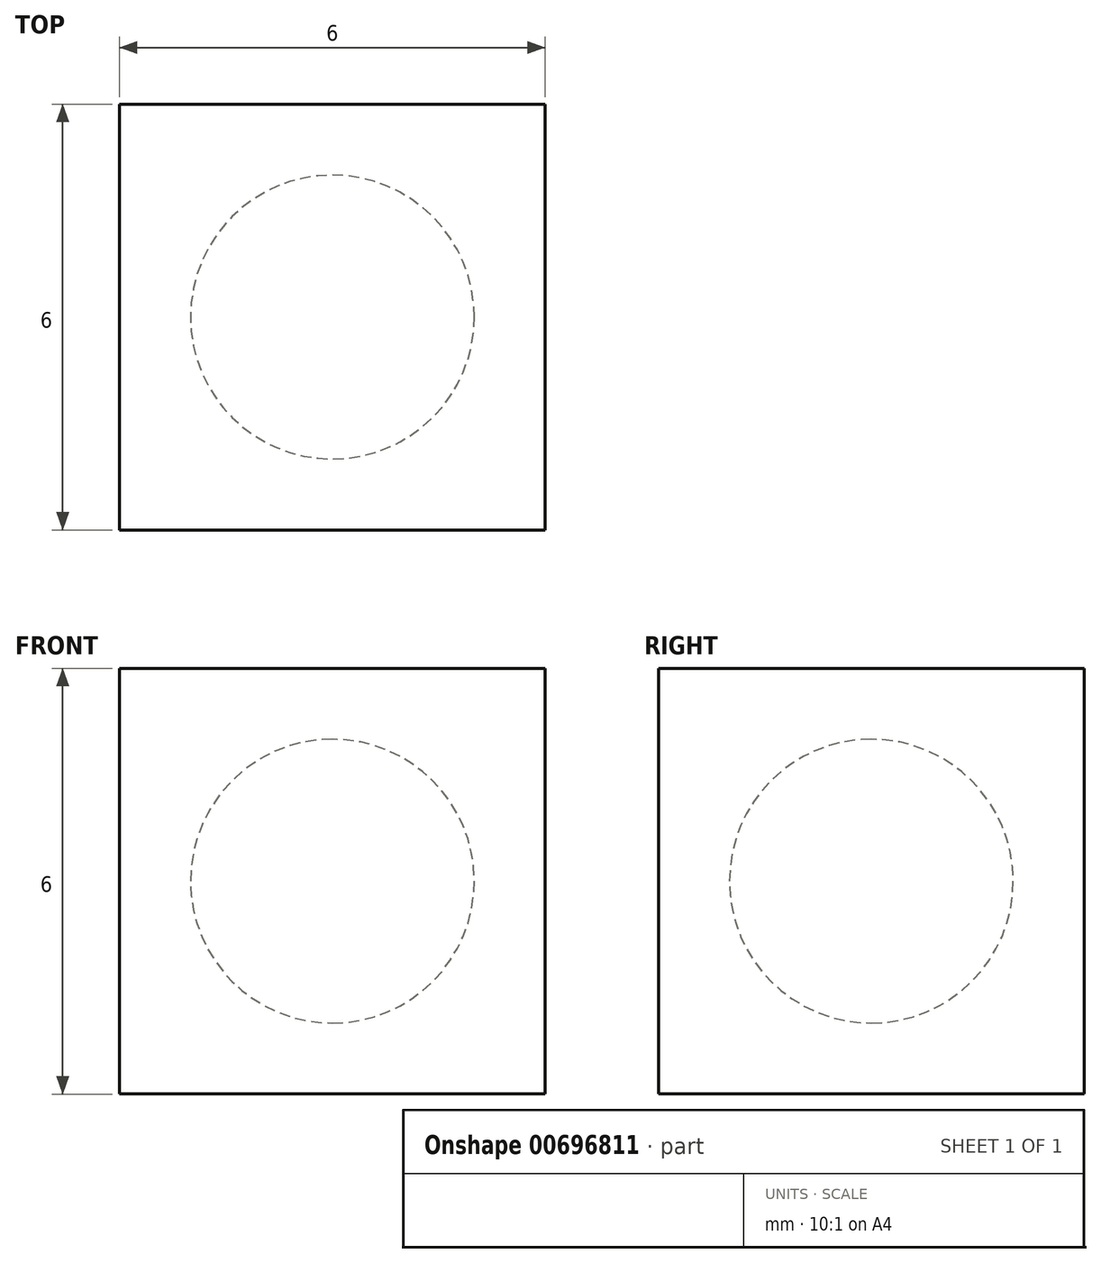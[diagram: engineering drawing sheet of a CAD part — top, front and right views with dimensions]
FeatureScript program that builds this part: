
annotation { "Feature Type Name" : "Feature", "Feature Type Description" : "" }
export const myFeature = defineFeature(function(context is Context, id is Id, definition is map)
    precondition{}
    {
        {
            var Q0;
            Q0=qCreatedBy(makeId("Front.planeOp"),FACE);
            var sketch = newSketch(context, id + "F0", { "sketchPlane" : qUnion([Q0])});
            skLineSegment(sketch, "E0.bottom", {"start": v(0.4, -1.79) * mm, "end": v(6.4, -1.79) * mm});
            skLineSegment(sketch, "E0.top", {"start": v(0.4, -7.79) * mm, "end": v(6.4, -7.79) * mm});
            skLineSegment(sketch, "E0.left", {"start": v(0.4, -1.79) * mm, "end": v(0.4, -7.79) * mm});
            skLineSegment(sketch, "E0.right", {"start": v(6.4, -1.79) * mm, "end": v(6.4, -7.79) * mm});
            skSolve(sketch);
        }
        {
            var Q0;
            Q0=makeQuery(id+"F0.imprint","IMPRINT",FACE,{"disambiguationData":[TD([[makeQuery(id+"F0.imprint","IMPRINT",EDGE,{"derivedFrom":sQuery(id+"F0.wireOp",EDGE,"E0.bottom")}),-1.0]])]});
            extrude(context, id + "F1", {"entities" : qUnion([Q0]), "depth" : 3 * mm, "offsetDistance" : 25.4 * mm});
        }
        {
            var Q0;
            Q0=makeQuery(id+"F1.opExtrude","CAP_FACE",FACE,{"disambiguationData":[OSD([sQuery(id+"F0.wireOp",EDGE,"E0.bottom"),sQuery(id+"F0.wireOp",EDGE,"E0.top"),sQuery(id+"F0.wireOp",EDGE,"E0.left"),sQuery(id+"F0.wireOp",EDGE,"E0.right")])],"isStart":false});
            var sketch = newSketch(context, id + "F2", { "sketchPlane" : qUnion([Q0])});
            skLineSegment(sketch, "E1", {"start": v(3.4, -2.79) * mm, "end": v(3.4, -6.79) * mm});
            skArc(sketch, "E2", {"start": v(3.4, -6.79) * mm, "mid": v(5.4, -4.79) * mm, "end": v(3.4, -2.79) * mm});
            skPoint(sketch, "E3.orphan", {"position": v(3.4, -1.79) * mm});
            skPoint(sketch, "E4.orphan", {"position": v(3.4, -7.79) * mm});
            skSolve(sketch);
        }
        {
            var Q0;
            Q0=makeQuery(id+"F2.imprint","IMPRINT",FACE,{"disambiguationData":[TD([[makeQuery(id+"F2.imprint","IMPRINT",EDGE,{"derivedFrom":sQuery(id+"F2.wireOp",EDGE,"E1")}),1.0]])]});
            var Q1;
            Q1=sQuery(id+"F2.wireOp",EDGE,"E1");
            revolve(context, id + "F3", {"operationType" : NewBodyOperationType.REMOVE, "entities" : qUnion([Q0]), "axis" : qUnion([Q1]), "revolveType" : RevolveType.ONE_DIRECTION, "oppositeDirection" : true, "angle" : 180 * degree});
        }
        {
            var Q0;
            Q0=makeQuery(id+"F1.opExtrude","SWEPT_BODY",BODY,{"disambiguationData":[OSD([sQuery(id+"F0.wireOp",EDGE,"E0.bottom"),sQuery(id+"F0.wireOp",EDGE,"E0.top"),sQuery(id+"F0.wireOp",EDGE,"E0.left"),sQuery(id+"F0.wireOp",EDGE,"E0.right")])]});
            var Q1;
            Q1=makeQuery(id+"F1.opExtrude","CAP_FACE",FACE,{"disambiguationData":[OSD([sQuery(id+"F0.wireOp",EDGE,"E0.bottom"),sQuery(id+"F0.wireOp",EDGE,"E0.top"),sQuery(id+"F0.wireOp",EDGE,"E0.left"),sQuery(id+"F0.wireOp",EDGE,"E0.right")])],"isStart":false});
            mirror(context, id + "F4", {"operationType" : NewBodyOperationType.ADD, "entities" : qUnion([Q0]), "mirrorPlane" : qUnion([Q1])});
        }
    });
